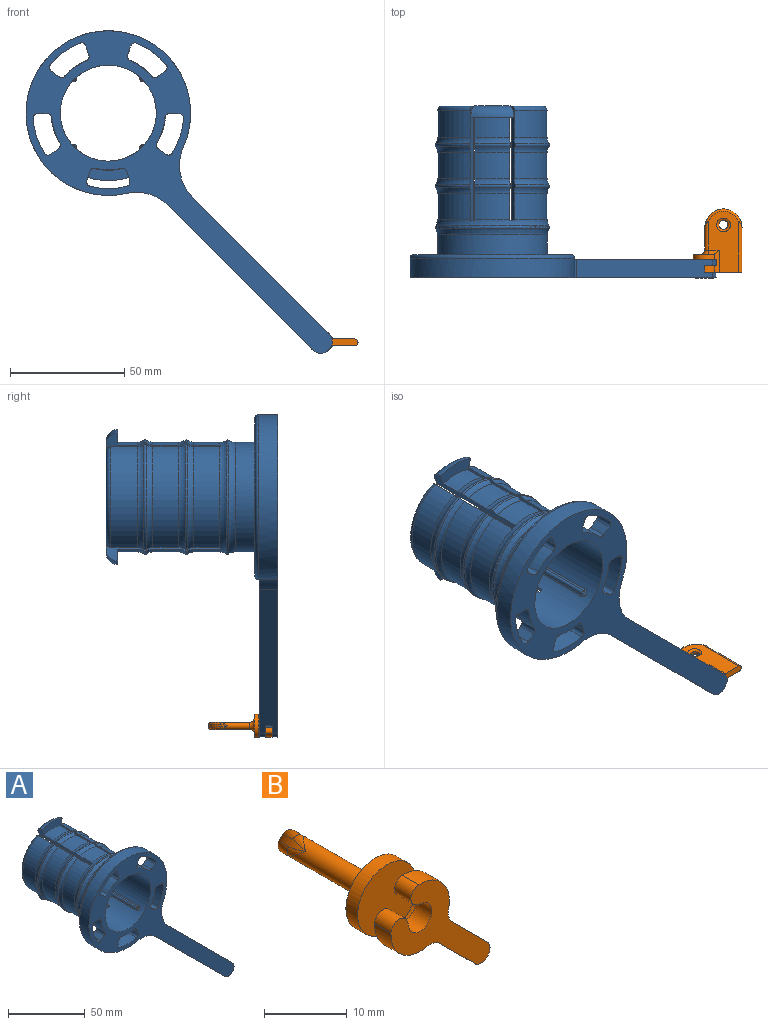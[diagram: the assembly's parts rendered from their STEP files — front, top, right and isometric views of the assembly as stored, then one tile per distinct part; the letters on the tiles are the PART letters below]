
ASSEMBLY  parts=2 mates=1
PART A: 142 faces, bbox 136.9x75x144 mm
  f0: plane 63.03x63.03mm, normal (-0.71,0,-0.71), area 698.1mm2, adj f65,f67,f69,f136,f137,f138,f139,f140
  f1: cylinder r=24mm len=15.24mm, axis (0,-1,0), area 134.6mm2, adj f11,f54,f55,f56
  f2: cylinder r=24mm len=43.98mm, axis (0,-1,0), area 649.8mm2, adj f12,f50,f58,f63
  f3: cylinder r=24mm len=15.24mm, axis (0,-1,0), area 176.3mm2, adj f17,f22,f55,f56
  f4: cylinder r=24mm len=43.98mm, axis (0,-1,0), area 632.1mm2, adj f18,f22,f50,f58
  f5: cylinder r=24mm len=15.24mm, axis (0,-1,0), area 176.3mm2, adj f13,f15,f55,f56
  f6: cylinder r=24mm len=43.98mm, axis (0,-1,0), area 632.1mm2, adj f14,f16,f50,f58
  f7: torus R=24mm, axis (0,1,0), area 18.9mm2, adj f15,f17,f55,f56
  f8: torus R=24mm, axis (0,1,0), area 67.7mm2, adj f16,f18,f50,f58
  f9: torus R=24mm, axis (0,1,0), area 18.9mm2, adj f11,f13,f55,f56
  f10: torus R=24mm, axis (0,1,0), area 67.7mm2, adj f12,f14,f50,f58
  f11: torus R=29mm, axis (0,-1,0), area 45.9mm2, adj f1,f9,f55,f56
  f12: torus R=29mm, axis (0,-1,0), area 164.8mm2, adj f2,f10,f50,f58
  f13: torus R=29mm, axis (0,1,0), area 45.9mm2, adj f5,f9,f55,f56
  f14: torus R=29mm, axis (0,1,0), area 164.8mm2, adj f6,f10,f50,f58
  f15: torus R=29mm, axis (0,-1,0), area 45.9mm2, adj f5,f7,f55,f56
  f16: torus R=29mm, axis (0,-1,0), area 164.8mm2, adj f6,f8,f50,f58
  f17: torus R=29mm, axis (0,1,0), area 45.9mm2, adj f3,f7,f55,f56
  f18: torus R=29mm, axis (0,1,0), area 164.8mm2, adj f4,f8,f50,f58
  f19: plane 15.56x4.59mm, normal (0,1,0), area 51.4mm2, adj f21,f55,f56,f61
  f20: plane 40.32x13.59mm, normal (0,1,0), area 49.8mm2, adj f21,f50,f58,f63
  f21: cylinder r=21mm len=75mm, axis (0,-1,0), area 8588.3mm2, adj f19,f20,f32,f33,f46,f47,f49,f50
  f22: torus R=29mm, axis (0,-1,0), area 444.1mm2, adj f3,f4,f24,f35,f40,f46,f47,f49
  f23: cylinder r=24mm len=43.98mm, axis (0,-1,0), area 649.8mm2, adj f28,f52,f60,f62
  f24: cylinder r=24mm len=43.98mm, axis (0,-1,0), area 632.1mm2, adj f22,f31,f52,f60
  f25: cylinder r=24mm len=43.98mm, axis (0,-1,0), area 632.1mm2, adj f29,f30,f52,f60
  f26: torus R=24mm, axis (0,1,0), area 67.7mm2, adj f30,f31,f52,f60
  f27: torus R=24mm, axis (0,1,0), area 67.7mm2, adj f28,f29,f52,f60
  f28: torus R=29mm, axis (0,-1,0), area 164.8mm2, adj f23,f27,f52,f60
  f29: torus R=29mm, axis (0,1,0), area 164.8mm2, adj f25,f27,f52,f60
  f30: torus R=29mm, axis (0,-1,0), area 164.8mm2, adj f25,f26,f52,f60
  f31: torus R=29mm, axis (0,1,0), area 164.8mm2, adj f24,f26,f52,f60
  f32: plane 15.56x4.59mm, normal (0,1,0), area 51.4mm2, adj f21,f46,f47,f53
  f33: plane 40.32x13.59mm, normal (0,1,0), area 49.8mm2, adj f21,f52,f60,f62
  f34: cylinder r=24mm len=15.24mm, axis (0,-1,0), area 134.6mm2, adj f42,f46,f47,f48
  f35: cylinder r=24mm len=15.24mm, axis (0,-1,0), area 176.3mm2, adj f22,f45,f46,f47
  f36: cylinder r=24mm len=15.24mm, axis (0,-1,0), area 176.3mm2, adj f43,f44,f46,f47
  f37: cylinder r=24mm len=48mm, axis (0,-1,0), area 1611mm2, adj f41,f71
  f38: torus R=24mm, axis (0,1,0), area 18.9mm2, adj f44,f45,f46,f47
  f39: torus R=24mm, axis (0,1,0), area 18.9mm2, adj f42,f43,f46,f47
  f40: torus R=24mm, axis (0,1,0), area 183.6mm2, adj f22,f41
  f41: torus R=29mm, axis (0,1,0), area 446.8mm2, adj f37,f40
  f42: torus R=29mm, axis (0,-1,0), area 45.9mm2, adj f34,f39,f46,f47
  f43: torus R=29mm, axis (0,1,0), area 45.9mm2, adj f36,f39,f46,f47
  f44: torus R=29mm, axis (0,-1,0), area 45.9mm2, adj f36,f38,f46,f47
  f45: torus R=29mm, axis (0,1,0), area 45.9mm2, adj f35,f38,f46,f47
  f46: plane 50x8.06mm, normal (-0.95,0,-0.32), area 177.2mm2, adj f21,f22,f32,f34,f35,f36,f38,f39
  f47: plane 50x8.06mm, normal (0.95,0,-0.32), area 177.2mm2, adj f21,f22,f32,f34,f35,f36,f38,f39
  f48: plane 18.73x6.74mm, normal (0,-1,0), area 95.1mm2, adj f34,f46,f47,f53
  f49: plane 3.53x2.95mm, normal (0,1,0), area 6mm2, adj f21,f22,f46,f50
  f50: plane 50x3.67mm, normal (0.92,0,0.4), area 154.2mm2, adj f2,f4,f6,f8,f10,f12,f14,f16
  f51: plane 3.53x2.95mm, normal (0,1,0), area 6mm2, adj f21,f22,f47,f52
  f52: plane 50x3.67mm, normal (-0.92,0,0.4), area 154.2mm2, adj f21,f22,f23,f24,f25,f26,f27,f28
  f53: torus R=24.5mm, axis (0,1,0), area 140.5mm2, adj f32,f46,f47,f48
  f54: plane 18.73x6.74mm, normal (0,-1,0), area 95.1mm2, adj f1,f55,f56,f61
  f55: plane 50x8.06mm, normal (0.95,0,0.32), area 177.2mm2, adj f1,f3,f5,f7,f9,f11,f13,f15
  f56: plane 50x8.06mm, normal (-0.95,0,0.32), area 177.2mm2, adj f1,f3,f5,f7,f9,f11,f13,f15
  f57: plane 3.53x2.95mm, normal (0,1,0), area 6mm2, adj f21,f22,f56,f58
  f58: plane 50x3.67mm, normal (0.92,0,-0.4), area 154.2mm2, adj f2,f4,f6,f8,f10,f12,f14,f16
  f59: plane 3.53x2.95mm, normal (0,1,0), area 6mm2, adj f21,f22,f55,f60
  f60: plane 50x3.67mm, normal (-0.92,0,-0.4), area 154.2mm2, adj f21,f22,f23,f24,f25,f26,f27,f28
  f61: torus R=24.5mm, axis (0,1,0), area 140.5mm2, adj f19,f54,f55,f56
  f62: torus R=22mm, axis (0,1,0), area 169.4mm2, adj f23,f33,f52,f60
  f63: torus R=22mm, axis (0,1,0), area 169.4mm2, adj f2,f20,f50,f58
  f64: cylinder r=36mm len=72mm, axis (0,1,0), area 1654.7mm2, adj f65,f67,f68,f69,f72
  f65: plane 90.31x90.07mm, normal (0,1,0), area 1117.8mm2, adj f0,f64,f66,f68,f69,f139
  f66: plane 59.48x59.48mm, normal (0.71,0,0.71), area 657.9mm2, adj f65,f67,f68,f136,f137,f138,f139,f140
  f67: plane 141x133.93mm, normal (0,-1,0), area 3096.4mm2, adj f0,f21,f64,f66,f68,f69,f70,f73
  f68: cylinder r=20mm len=22.3mm, axis (0,1,0), area 192.9mm2, adj f64,f65,f66,f67
  f69: cylinder r=20mm len=18.51mm, axis (0,1,0), area 160.9mm2, adj f0,f64,f65,f67
  f70: cylinder r=33mm len=66mm, axis (0,1,0), area 743.2mm2, adj f67,f71,f72,f77,f78,f84,f85,f91
  f71: plane 66x65.04mm, normal (0,1,0), area 904.2mm2, adj f37,f70,f73,f74,f75,f76,f77,f78
  f72: torus R=34.5mm, axis (0,-1,0), area 1021.5mm2, adj f64,f70
  f73: cylinder r=24.83mm len=11.43mm, axis (0,1,0), area 92.3mm2, adj f67,f71,f76,f79
  f74: plane 8x3.98mm, normal (-0.95,0,-0.3), area 33.4mm2, adj f67,f71,f76,f77
  f75: plane 8x3.98mm, normal (0.95,0,-0.3), area 33.4mm2, adj f67,f71,f78,f79
  f76: cylinder r=2mm len=8mm, axis (0,1,0), area 23.9mm2, adj f67,f71,f73,f74
  f77: cylinder r=2mm len=8mm, axis (0,1,0), area 26.2mm2, adj f67,f70,f71,f74
  f78: cylinder r=2mm len=8mm, axis (0,1,0), area 26.2mm2, adj f67,f70,f71,f75
  f79: cylinder r=2mm len=8mm, axis (0,1,0), area 23.9mm2, adj f67,f71,f73,f75
  f80: cylinder r=24.83mm len=10.87mm, axis (0,1,0), area 92.3mm2, adj f67,f71,f83,f86
  f81: plane 8x3.4mm, normal (-0.58,0,0.81), area 33.4mm2, adj f67,f71,f83,f84
  f82: plane 8x4.18mm, normal (0.01,0,-1), area 33.4mm2, adj f67,f71,f85,f86
  f83: cylinder r=2mm len=8mm, axis (0,1,0), area 23.9mm2, adj f67,f71,f80,f81
  f84: cylinder r=2mm len=8mm, axis (0,1,0), area 26.2mm2, adj f67,f70,f71,f81
  f85: cylinder r=2mm len=8mm, axis (0,1,0), area 26.2mm2, adj f67,f70,f71,f82
  f86: cylinder r=2mm len=8mm, axis (0,1,0), area 23.9mm2, adj f67,f71,f80,f82
  f87: cylinder r=24.83mm len=9.25mm, axis (0,1,0), area 92.3mm2, adj f67,f71,f90,f93
  f88: plane 8x3.36mm, normal (0.59,0,0.8), area 33.4mm2, adj f67,f71,f90,f91
  f89: plane 8x3.96mm, normal (-0.95,0,-0.32), area 33.4mm2, adj f67,f71,f92,f93
  f90: cylinder r=2mm len=8mm, axis (0,1,0), area 23.9mm2, adj f67,f71,f87,f88
  f91: cylinder r=2mm len=8mm, axis (0,1,0), area 26.2mm2, adj f67,f70,f71,f88
  f92: cylinder r=2mm len=8mm, axis (0,1,0), area 26.2mm2, adj f67,f70,f71,f89
  f93: cylinder r=2mm len=8mm, axis (0,1,0), area 23.9mm2, adj f67,f71,f87,f89
  f94: cylinder r=24.83mm len=9.25mm, axis (0,1,0), area 92.3mm2, adj f67,f71,f97,f100
  f95: plane 8x3.96mm, normal (0.95,0,-0.32), area 33.4mm2, adj f67,f71,f97,f98
  f96: plane 8x3.36mm, normal (-0.59,0,0.8), area 33.4mm2, adj f67,f71,f99,f100
  f97: cylinder r=2mm len=8mm, axis (0,1,0), area 23.9mm2, adj f67,f71,f94,f95
  f98: cylinder r=2mm len=8mm, axis (0,1,0), area 26.2mm2, adj f67,f70,f71,f95
  f99: cylinder r=2mm len=8mm, axis (0,1,0), area 26.2mm2, adj f67,f70,f71,f96
  f100: cylinder r=2mm len=8mm, axis (0,1,0), area 23.9mm2, adj f67,f71,f94,f96
  f101: cylinder r=24.83mm len=10.87mm, axis (0,1,0), area 92.3mm2, adj f67,f71,f104,f107
  f102: plane 8x4.18mm, normal (-0.01,0,-1), area 33.4mm2, adj f67,f71,f104,f105
  f103: plane 8x3.4mm, normal (0.58,0,0.81), area 33.4mm2, adj f67,f71,f106,f107
  f104: cylinder r=2mm len=8mm, axis (0,1,0), area 23.9mm2, adj f67,f71,f101,f102
  f105: cylinder r=2mm len=8mm, axis (0,1,0), area 26.2mm2, adj f67,f70,f71,f102
  f106: cylinder r=2mm len=8mm, axis (0,1,0), area 26.2mm2, adj f67,f70,f71,f103
  f107: cylinder r=2mm len=8mm, axis (0,1,0), area 23.9mm2, adj f67,f71,f101,f103
  f108: cylinder r=1mm len=63mm, axis (0,-1,0), area 126.7mm2, adj f118,f119,f120,f123
  f109: cylinder r=1mm len=63mm, axis (0,-1,0), area 126.7mm2, adj f116,f117,f124,f127
  f110: cylinder r=1mm len=63mm, axis (0,-1,0), area 126.7mm2, adj f114,f115,f128,f131
  f111: cylinder r=1mm len=63mm, axis (0,-1,0), area 126.7mm2, adj f112,f113,f132,f135
  f112: sphere r=1mm, area 1.5mm2, adj f111,f133
  f113: sphere r=1mm, area 1.5mm2, adj f111,f134
  f114: sphere r=1mm, area 1.5mm2, adj f110,f129
  f115: sphere r=1mm, area 1.5mm2, adj f110,f130
  f116: sphere r=1mm, area 1.5mm2, adj f109,f125
  f117: sphere r=1mm, area 1.5mm2, adj f109,f126
  f118: sphere r=1mm, area 1.5mm2, adj f108,f122
  f119: sphere r=1mm, area 1.5mm2, adj f108,f121
  f120: cylinder r=1mm len=63mm, axis (0,-1,0), area 68.7mm2, adj f21,f108,f121,f122
  f121: bspline ~2.51x2.51mm, area 4.2mm2, adj f21,f119,f120,f123
  f122: bspline ~2.51x2.51mm, area 4.2mm2, adj f21,f118,f120,f123
  f123: cylinder r=1mm len=63mm, axis (0,1,0), area 68.7mm2, adj f21,f108,f121,f122
  f124: cylinder r=1mm len=63mm, axis (0,1,0), area 68.7mm2, adj f21,f109,f125,f126
  f125: bspline ~2.51x2.51mm, area 4.2mm2, adj f21,f116,f124,f127
  f126: bspline ~2.51x2.51mm, area 4.2mm2, adj f21,f117,f124,f127
  f127: cylinder r=1mm len=63mm, axis (0,-1,0), area 68.7mm2, adj f21,f109,f125,f126
  f128: cylinder r=1mm len=63mm, axis (0,1,0), area 68.7mm2, adj f21,f110,f129,f130
  f129: bspline ~2.51x2.51mm, area 4.2mm2, adj f21,f114,f128,f131
  f130: bspline ~2.51x2.51mm, area 4.2mm2, adj f21,f115,f128,f131
  f131: cylinder r=1mm len=63mm, axis (0,-1,0), area 68.7mm2, adj f21,f110,f129,f130
  f132: cylinder r=1mm len=63mm, axis (0,1,0), area 68.7mm2, adj f21,f111,f133,f134
  f133: bspline ~2.51x2.51mm, area 4.2mm2, adj f21,f112,f132,f135
  f134: bspline ~2.51x2.51mm, area 4.2mm2, adj f21,f113,f132,f135
  f135: cylinder r=1mm len=63mm, axis (0,-1,0), area 68.7mm2, adj f21,f111,f133,f134
  f136: plane 12.07x12.07mm, normal (0,1,0), area 76.7mm2, adj f0,f66,f138,f140,f141
  f137: plane 12.07x12.07mm, normal (0,-1,0), area 76.7mm2, adj f0,f66,f138,f139,f141
  f138: plane 7.07x7.07mm, normal (0.71,0,-0.71), area 30mm2, adj f0,f66,f136,f137
  f139: cylinder r=5mm len=8.54mm, axis (0,-1,0), area 39.3mm2, adj f0,f65,f66,f137
  f140: cylinder r=5mm len=8.54mm, axis (0,-1,0), area 39.3mm2, adj f0,f66,f67,f136
  f141: cylinder r=2mm len=4mm, axis (0,-1,0), area 37.7mm2, adj f136,f137
PART B: 30 faces, bbox 17.2x28.4x17.2 mm
  f0: plane 26.7x9.38mm, normal (-0.71,0,-0.71), area 263.3mm2, adj f1,f2,f8,f12,f21,f26,f28
  f1: cylinder r=1.5mm len=12.49mm, axis (0,-1,0), area 53.1mm2, adj f0,f18,f20,f25
  f2: cylinder r=1.5mm len=22.19mm, axis (0,-1,0), area 98.8mm2, adj f0,f8,f18,f24
  f3: plane 10x10mm, normal (0,1,0), area 58.5mm2, adj f4,f5,f6,f7,f9,f10,f11,f12
  f4: cylinder r=5mm len=6.15mm, axis (0,-1,0), area 25.9mm2, adj f3,f5,f8,f13
  f5: cylinder r=1.42mm len=2.8mm, axis (0,-1,0), area 9.2mm2, adj f3,f4,f8,f10
  f6: cylinder r=5mm len=6.15mm, axis (0,-1,0), area 25.9mm2, adj f3,f7,f8,f12
  f7: cylinder r=1.42mm len=2.8mm, axis (0,-1,0), area 9.2mm2, adj f3,f6,f8,f9
  f8: plane 16.94x16.94mm, normal (0,-1,0), area 90.6mm2, adj f0,f2,f4,f5,f6,f7,f9,f10
  f9: cylinder r=2mm len=2.8mm, axis (0,-1,0), area 4mm2, adj f3,f7,f8,f11
  f10: cylinder r=2mm len=2.8mm, axis (0,-1,0), area 4mm2, adj f3,f5,f8,f11
  f11: cylinder r=2mm len=4mm, axis (0,-1,0), area 25.7mm2, adj f3,f8,f9,f10
  f12: cylinder r=2.37mm len=9.7mm, axis (0,-1,0), area 17.8mm2, adj f0,f3,f6,f8,f14,f15,f16,f21
  f13: cylinder r=2.37mm len=9.7mm, axis (0,-1,0), area 17.8mm2, adj f3,f4,f8,f14,f15,f16,f18,f19
  f14: cylinder r=5.4mm len=2.9mm, axis (0,-1,0), area 10.8mm2, adj f3,f12,f13,f15
  f15: plane 10x10mm, normal (0,-1,0), area 80.2mm2, adj f12,f13,f14,f16
  f16: cylinder r=5mm len=10mm, axis (0,-1,0), area 52mm2, adj f12,f13,f15,f17,f19,f21
  f17: plane 10x10mm, normal (0,1,0), area 37.9mm2, adj f16,f19,f20,f21
  f18: plane 26.7x9.38mm, normal (0.71,0,0.71), area 263.3mm2, adj f1,f2,f8,f13,f19,f23,f29
  f19: cylinder r=2mm len=4.79mm, axis (0.71,0,-0.71), area 10.6mm2, adj f13,f16,f17,f18,f20
  f20: torus R=3.5mm, axis (0,1,0), area 22mm2, adj f1,f17,f19,f21
  f21: cylinder r=2mm len=4.79mm, axis (-0.71,0,0.71), area 10.6mm2, adj f0,f12,f16,f17,f20
  f22: cylinder r=8.14mm len=12.21mm, axis (0.71,0,0.71), area 23.7mm2, adj f23,f24,f25,f26
  f23: torus R=7.14mm, axis (-0.71,0,-0.71), area 29.2mm2, adj f18,f22,f24,f25
  f24: bspline ~3.53x3.13mm, area 4.9mm2, adj f2,f22,f23,f26
  f25: bspline ~3.53x3.13mm, area 4.9mm2, adj f1,f22,f23,f26
  f26: torus R=7.14mm, axis (0.71,0,0.71), area 29.2mm2, adj f0,f22,f24,f25
  f27: cylinder r=2mm len=4mm, axis (0.71,0,0.71), area 12.6mm2, adj f28,f29
  f28: torus R=3mm, axis (0.71,0,0.71), area 23.3mm2, adj f0,f27
  f29: torus R=3mm, axis (-0.71,0,-0.71), area 23.3mm2, adj f18,f27
PLACE A t=(-32.35,31.34,-10.12)mm fixed
PLACE B rot(axis=(0,-1,0),43.9deg) t=(-75.72,31.34,-102.52)mm
MATE revolute A.f139 <-> B.f14  axis (0,-1,0) through (60.58,20.84,-110.12)mm
